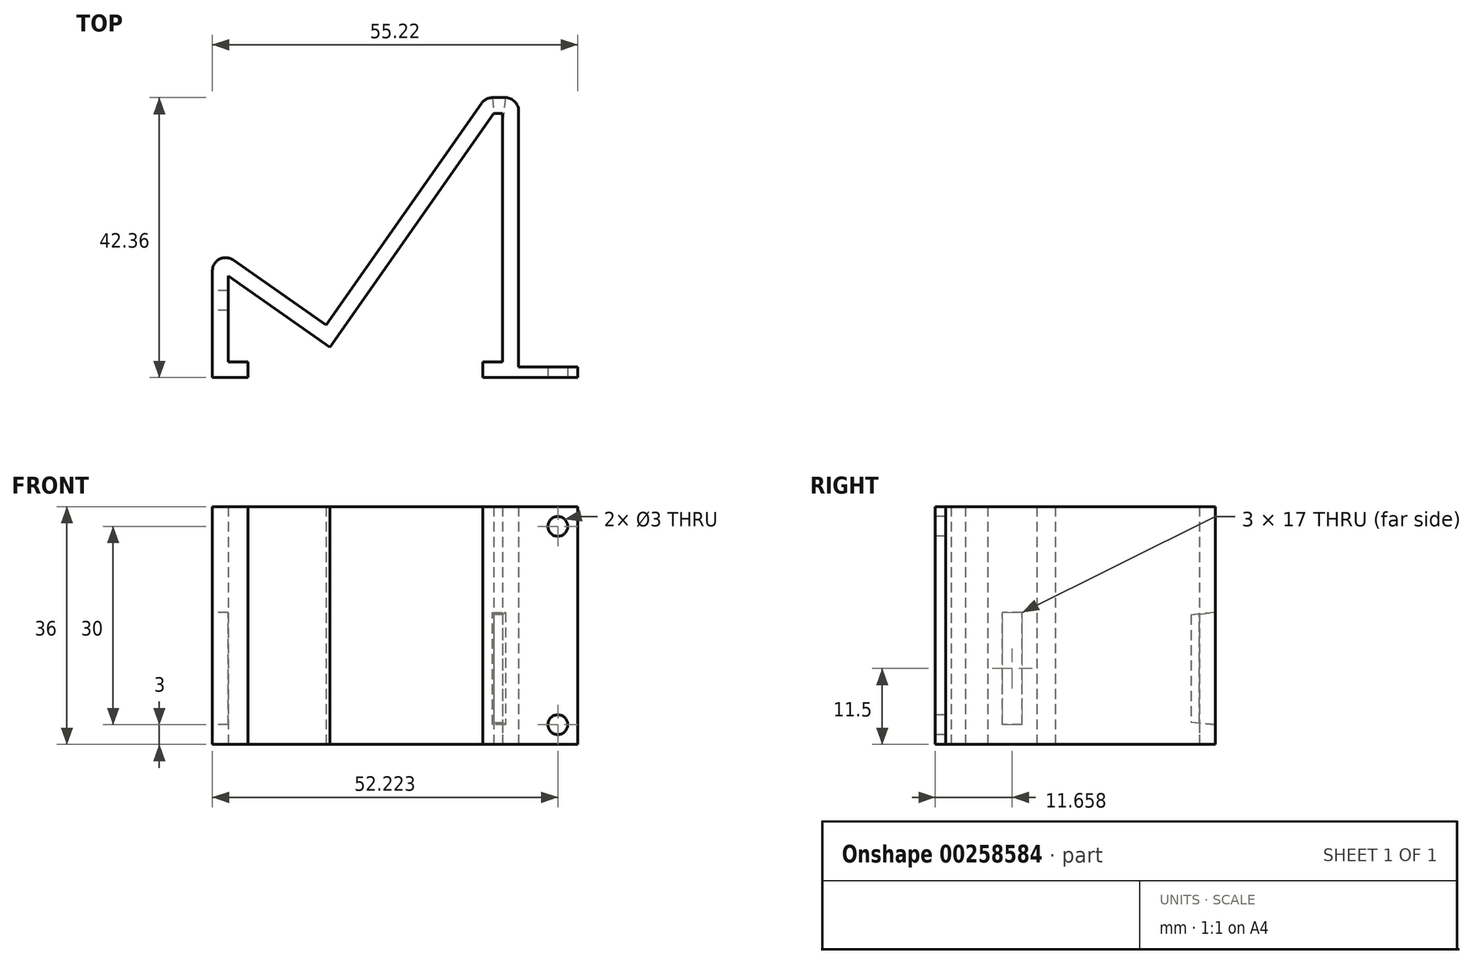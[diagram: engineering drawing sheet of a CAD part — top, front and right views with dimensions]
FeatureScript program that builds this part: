
annotation { "Feature Type Name" : "Feature", "Feature Type Description" : "" }
export const myFeature = defineFeature(function(context is Context, id is Id, definition is map)
    precondition{}
    {
        {
            var Q0;
            Q0=qCreatedBy(makeId("Top.planeOp"),FACE);
            var sketch = newSketch(context, id + "F0", { "sketchPlane" : qUnion([Q0])});
            skLineSegment(sketch, "E0", {"start": v(0, 0) * mm, "end": v(0, 16.16) * mm});
            skLineSegment(sketch, "E1", {"start": v(3.15, 17.8) * mm, "end": v(17.2, 7.95) * mm});
            skLineSegment(sketch, "E2", {"start": v(17.2, 7.95) * mm, "end": v(40.7, 41.5) * mm});
            skLineSegment(sketch, "E3", {"start": v(42.33, 42.36) * mm, "end": v(44.3, 42.36) * mm});
            skLineSegment(sketch, "E4", {"start": v(46.3, 40.36) * mm, "end": v(46.3, 0) * mm});
            skLineSegment(sketch, "E5", {"start": v(46.3, 0) * mm, "end": v(0, 0) * mm});
            skPoint(sketch, "E6.visualSharp", {"position": v(0, 20) * mm});
            skArc(sketch, "E6.filletArc", {"start": v(3.15, 17.8) * mm, "mid": v(1.08, 17.93) * mm, "end": v(0, 16.16) * mm});
            skPoint(sketch, "E7.visualSharp", {"position": v(41.3, 42.36) * mm});
            skArc(sketch, "E7.filletArc", {"start": v(42.33, 42.36) * mm, "mid": v(41.41, 42.13) * mm, "end": v(40.7, 41.5) * mm});
            skPoint(sketch, "E8.visualSharp", {"position": v(46.3, 42.36) * mm});
            skArc(sketch, "E8.filletArc", {"start": v(46.3, 40.36) * mm, "mid": v(45.7, 41.77) * mm, "end": v(44.3, 42.36) * mm});
            skLineSegment(sketch, "E9.0", {"start": v(2.4, 15.39) * mm, "end": v(17.8, 4.61) * mm});
            skLineSegment(sketch, "E9.1", {"start": v(42.54, 39.96) * mm, "end": v(43.9, 39.96) * mm});
            skLineSegment(sketch, "E9.2", {"start": v(43.9, 39.96) * mm, "end": v(43.9, 2.4) * mm});
            skLineSegment(sketch, "E9.3", {"start": v(17.8, 4.61) * mm, "end": v(42.54, 39.96) * mm});
            skLineSegment(sketch, "E9.4", {"start": v(43.9, 2.4) * mm, "end": v(2.4, 2.4) * mm});
            skLineSegment(sketch, "E9.5", {"start": v(2.4, 2.4) * mm, "end": v(2.4, 15.39) * mm});
            skLineSegment(sketch, "E10", {"start": v(43.9, 2.4) * mm, "end": v(40.9, 2.4) * mm});
            skLineSegment(sketch, "E11", {"start": v(40.9, 2.4) * mm, "end": v(40.9, 0) * mm});
            skLineSegment(sketch, "E12", {"start": v(2.4, 2.4) * mm, "end": v(5.4, 2.4) * mm});
            skLineSegment(sketch, "E13", {"start": v(5.4, 2.4) * mm, "end": v(5.4, 0) * mm});
            skSolve(sketch);
        }
        {
            var Q0;
            {var subQ1=sQuery(id+"F0.wireOp",EDGE,"E0");Q0=makeQuery(id+"F0.imprint","IMPRINT",FACE,{"disambiguationData":[TD([[makeQuery(id+"F0.imprint","IMPRINT",EDGE,{"derivedFrom":subQ1}),-1.0]])]});}
            extrude(context, id + "F1", {"entities" : qUnion([Q0]), "depth" : 36 * mm});
        }
        {
            var Q0;
            {var subQ0=sQuery(id+"F0.wireOp",EDGE,"E5");Q0=makeQuery(id+"F1.opExtrude","SWEPT_FACE",FACE,{"disambiguationData":[OSD([subQ0]),TDD([makeQuery(id+"F0.imprint","IMPRINT",EDGE,{"disambiguationData":[TD([[makeQuery(id+"F0.imprint","INTERSECT",VERTEX,{"derivedFrom":[sQuery(id+"F0.wireOp",EDGE,"E0"),subQ0]}),1.0]])],"derivedFrom":subQ0})])]});}
            var sketch = newSketch(context, id + "F2", { "sketchPlane" : qUnion([Q0])});
            skLineSegment(sketch, "E14", {"start": v(0, 0) * mm, "end": v(46.22, 0) * mm});
            skLineSegment(sketch, "E15.bottom", {"start": v(55.22, 0) * mm, "end": v(-10.78, 0) * mm});
            skLineSegment(sketch, "E15.top", {"start": v(55.22, 36) * mm, "end": v(-10.78, 36) * mm});
            skLineSegment(sketch, "E15.left", {"start": v(55.22, 0) * mm, "end": v(55.22, 36) * mm});
            skLineSegment(sketch, "E15.right", {"start": v(-10.78, 0) * mm, "end": v(-10.78, 36) * mm});
            skPoint(sketch, "E15.middle", {"position": v(22.22, 18) * mm});
            skLineSegment(sketch, "E16.bottom", {"start": v(5.4, 0) * mm, "end": v(42.18, 0) * mm});
            skLineSegment(sketch, "E16.top", {"start": v(5.4, 36) * mm, "end": v(42.18, 36) * mm});
            skLineSegment(sketch, "E16.left", {"start": v(5.4, 0) * mm, "end": v(5.4, 36) * mm});
            skLineSegment(sketch, "E16.right", {"start": v(42.18, 0) * mm, "end": v(42.18, 36) * mm});
            skLineSegment(sketch, "E17.bottom", {"start": v(-10.78, 0) * mm, "end": v(-7.78, 0) * mm});
            skLineSegment(sketch, "E17.top", {"start": v(-10.78, 3) * mm, "end": v(-7.78, 3) * mm, "construction": true});
            skLineSegment(sketch, "E17.left", {"start": v(-10.78, 0) * mm, "end": v(-10.78, 3) * mm});
            skLineSegment(sketch, "E17.right", {"start": v(-7.78, 0) * mm, "end": v(-7.78, 3) * mm, "construction": true});
            skLineSegment(sketch, "E18.bottom", {"start": v(-7.78, 3) * mm, "end": v(52.22, 3) * mm, "construction": true});
            skLineSegment(sketch, "E18.top", {"start": v(-7.78, 33) * mm, "end": v(52.22, 33) * mm, "construction": true});
            skLineSegment(sketch, "E18.left", {"start": v(-7.78, 3) * mm, "end": v(-7.78, 33) * mm, "construction": true});
            skLineSegment(sketch, "E18.right", {"start": v(52.22, 3) * mm, "end": v(52.22, 33) * mm, "construction": true});
            skCircle(sketch, "E19", {"center": v(-7.78, 33) * mm, "radius": 1.5 * mm});
            skCircle(sketch, "E20", {"center": v(-7.78, 3) * mm, "radius": 1.5 * mm});
            skCircle(sketch, "E21", {"center": v(52.22, 33) * mm, "radius": 1.5 * mm});
            skCircle(sketch, "E22", {"center": v(52.22, 3) * mm, "radius": 1.5 * mm});
            skLineSegment(sketch, "E23", {"start": v(-10.78, 18) * mm, "end": v(-28.5, 18) * mm});
            skPoint(sketch, "E23.endSnap0", {"position": v(-10.78, 18) * mm});
            skCircle(sketch, "E24", {"center": v(-28.5, 18) * mm, "radius": 21.23 * mm});
            skSolve(sketch);
        }
        {
            var Q0;
            {var subQ9=sQuery(id+"F2.wireOp",EDGE,"E17.bottom");Q0=makeQuery(id+"F2.imprint","IMPRINT",FACE,{"disambiguationData":[TD([[makeQuery(id+"F2.imprint","IMPRINT",EDGE,{"derivedFrom":subQ9}),1.0]])]});}
            var Q1;
            {var subQ1=sQuery(id+"F2.wireOp",EDGE,"E15.left");Q1=makeQuery(id+"F2.imprint","IMPRINT",FACE,{"disambiguationData":[TD([[makeQuery(id+"F2.imprint","IMPRINT",EDGE,{"derivedFrom":subQ1}),1.0]])]});}
            extrude(context, id + "F3", {"entities" : qUnion([Q0, Q1]), "operationType" : NewBodyOperationType.ADD, "oppositeDirection" : true, "depth" : 1.6 * mm});
        }
        {
            var Q0;
            Q0=makeQuery(id+"F1.opExtrude","SWEPT_FACE",FACE,{"disambiguationData":[OSD([sQuery(id+"F0.wireOp",EDGE,"E0")])]});
            var sketch = newSketch(context, id + "F4", { "sketchPlane" : qUnion([Q0])});
            skLineSegment(sketch, "E25", {"start": v(-16.16, 0) * mm, "end": v(-13.16, 0) * mm});
            skLineSegment(sketch, "E26", {"start": v(-13.16, 0) * mm, "end": v(-13.16, 3) * mm});
            skLineSegment(sketch, "E27.bottom", {"start": v(-13.16, 3) * mm, "end": v(-10.16, 3) * mm});
            skLineSegment(sketch, "E27.top", {"start": v(-13.16, 20) * mm, "end": v(-10.16, 20) * mm});
            skLineSegment(sketch, "E27.left", {"start": v(-13.16, 3) * mm, "end": v(-13.16, 20) * mm});
            skLineSegment(sketch, "E27.right", {"start": v(-10.16, 3) * mm, "end": v(-10.16, 20) * mm});
            skSolve(sketch);
        }
        {
            var Q0;
            Q0=makeQuery(id+"F4.imprint","IMPRINT",FACE,{"disambiguationData":[TD([[makeQuery(id+"F4.imprint","IMPRINT",EDGE,{"derivedFrom":sQuery(id+"F4.wireOp",EDGE,"E27.bottom")}),1.0]])]});
            extrude(context, id + "F5", {"entities" : qUnion([Q0]), "operationType" : NewBodyOperationType.REMOVE, "oppositeDirection" : true, "depth" : 3 * mm});
        }
        {
            var Q0;
            Q0=makeQuery(id+"F1.opExtrude","SWEPT_FACE",FACE,{"disambiguationData":[OSD([sQuery(id+"F0.wireOp",EDGE,"E3")])]});
            var sketch = newSketch(context, id + "F6", { "sketchPlane" : qUnion([Q0])});
            skLineSegment(sketch, "E28", {"start": v(-44.3, 0) * mm, "end": v(-44.3, 3) * mm});
            skLineSegment(sketch, "E29.bottom", {"start": v(-44.3, 3) * mm, "end": v(-42.33, 3) * mm});
            skLineSegment(sketch, "E29.top", {"start": v(-44.3, 20) * mm, "end": v(-42.33, 20) * mm});
            skLineSegment(sketch, "E29.left", {"start": v(-44.3, 3) * mm, "end": v(-44.3, 20) * mm});
            skLineSegment(sketch, "E29.right", {"start": v(-42.33, 3) * mm, "end": v(-42.33, 20) * mm});
            skSolve(sketch);
        }
        {
            var Q0;
            Q0=makeQuery(id+"F6.imprint","IMPRINT",FACE,{"disambiguationData":[TD([[makeQuery(id+"F6.imprint","IMPRINT",EDGE,{"derivedFrom":sQuery(id+"F6.wireOp",EDGE,"E29.bottom")}),1.0]])]});
            extrude(context, id + "F7", {"entities" : qUnion([Q0]), "operationType" : NewBodyOperationType.REMOVE, "oppositeDirection" : true, "depth" : 4 * mm, "hasDraft" : true, "draftAngle" : 6.2 * degree, "draftPullDirection" : true});
        }
    });
